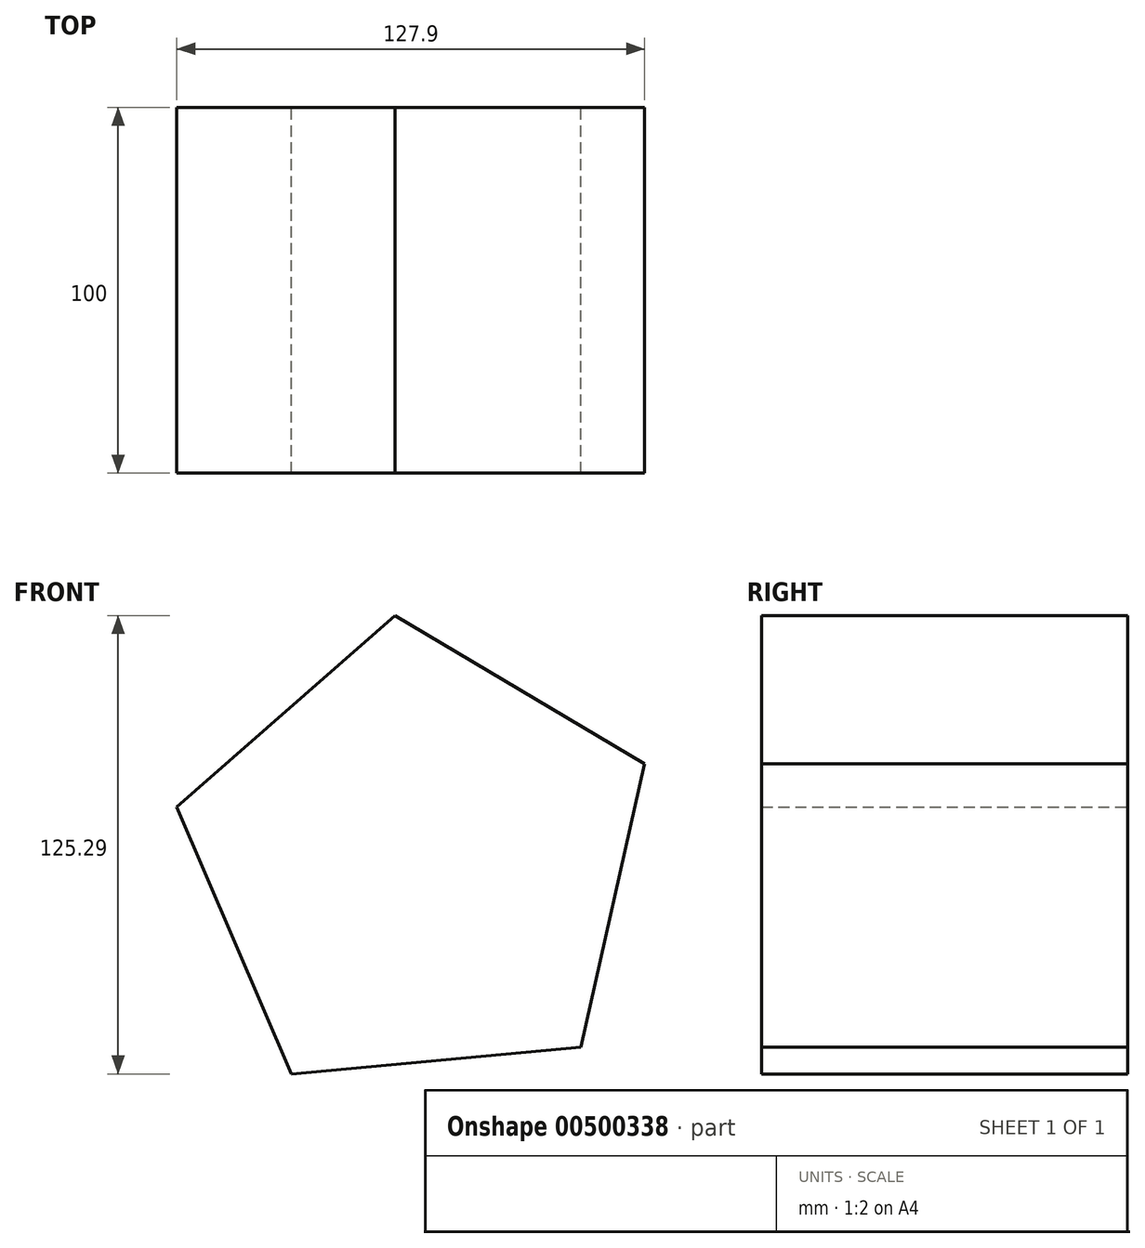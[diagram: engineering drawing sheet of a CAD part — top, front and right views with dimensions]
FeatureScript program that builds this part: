
annotation { "Feature Type Name" : "Feature", "Feature Type Description" : "" }
export const myFeature = defineFeature(function(context is Context, id is Id, definition is map)
    precondition{}
    {
        {
            var Q0;
            Q0=qCreatedBy(makeId("Front.planeOp"),FACE);
            var sketch = newSketch(context, id + "F0", { "sketchPlane" : qUnion([Q0])});
            skCircle(sketch, "E0.cCircle", {"center": v(0, 0) * mm, "radius": 67.53 * mm, "construction": true});
            skLineSegment(sketch, "E0.0", {"start": v(-34.5, -58.05) * mm, "end": v(-65.87, 14.87) * mm});
            skLineSegment(sketch, "E0.1", {"start": v(-65.87, 14.87) * mm, "end": v(-6.2, 67.24) * mm});
            skLineSegment(sketch, "E0.2", {"start": v(-6.2, 67.24) * mm, "end": v(62.03, 26.68) * mm});
            skLineSegment(sketch, "E0.3", {"start": v(62.03, 26.68) * mm, "end": v(44.55, -50.75) * mm});
            skLineSegment(sketch, "E0.4", {"start": v(44.55, -50.75) * mm, "end": v(-34.5, -58.05) * mm});
            skSolve(sketch);
        }
        {
            var Q0;
            Q0 = qSketchRegion(id + "F0", true);
            extrude(context, id + "F1", {"entities" : qUnion([Q0]), "depth" : 100 * mm});
        }
    });
